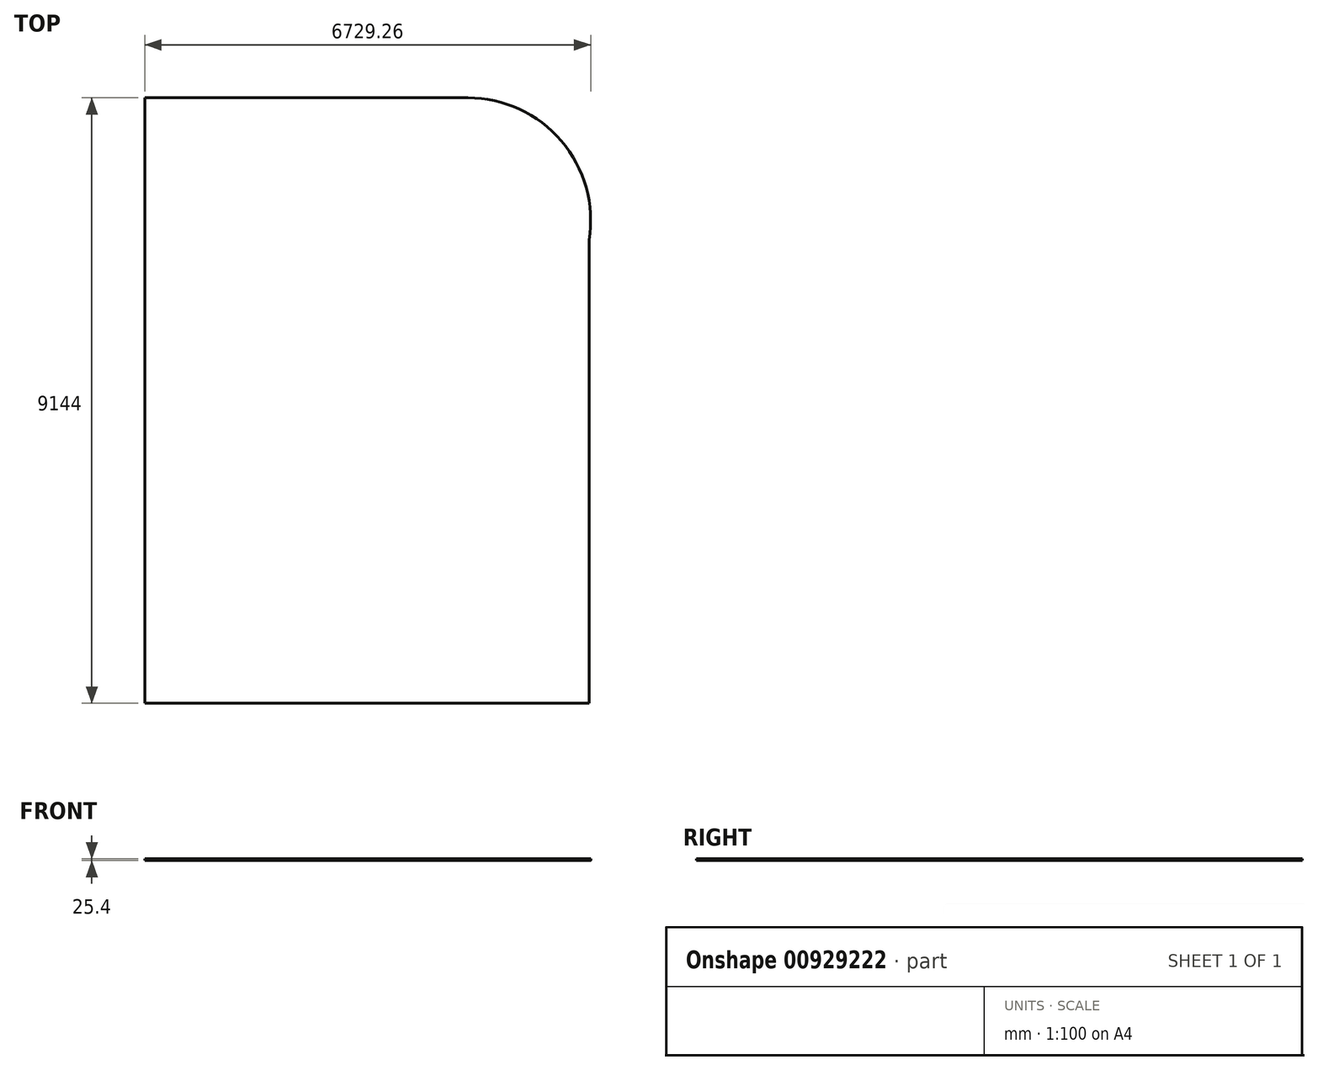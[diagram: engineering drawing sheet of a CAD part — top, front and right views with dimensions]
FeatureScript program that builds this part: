
annotation { "Feature Type Name" : "Feature", "Feature Type Description" : "" }
export const myFeature = defineFeature(function(context is Context, id is Id, definition is map)
    precondition{}
    {
        {
            var Q0;
            Q0=qCreatedBy(makeId("Top.planeOp"),FACE);
            var sketch = newSketch(context, id + "F0", { "sketchPlane" : qUnion([Q0])});
            skLineSegment(sketch, "E0.bottom", {"start": v(1524, 4572) * mm, "end": v(-3352.8, 4572) * mm});
            skLineSegment(sketch, "E0.top", {"start": v(3352.8, -4572) * mm, "end": v(-3352.8, -4572) * mm});
            skLineSegment(sketch, "E0.left", {"start": v(3352.8, 2743.2) * mm, "end": v(3352.8, -4572) * mm});
            skLineSegment(sketch, "E0.right", {"start": v(-3352.8, 4572) * mm, "end": v(-3352.8, -4572) * mm});
            skPoint(sketch, "E0.middle", {"position": v(0, 0) * mm});
            skArc(sketch, "E1", {"start": v(1524, 4572) * mm, "mid": v(2934.36, 3920.57) * mm, "end": v(3352.8, 2424.45) * mm});
            skSolve(sketch);
        }
        {
            var Q0;
            Q0 = qSketchRegion(id + "F0", true);
            extrude(context, id + "F1", {"entities" : qUnion([Q0]), "depth" : 25.4 * mm, "offsetDistance" : 25.4 * mm});
        }
    });
